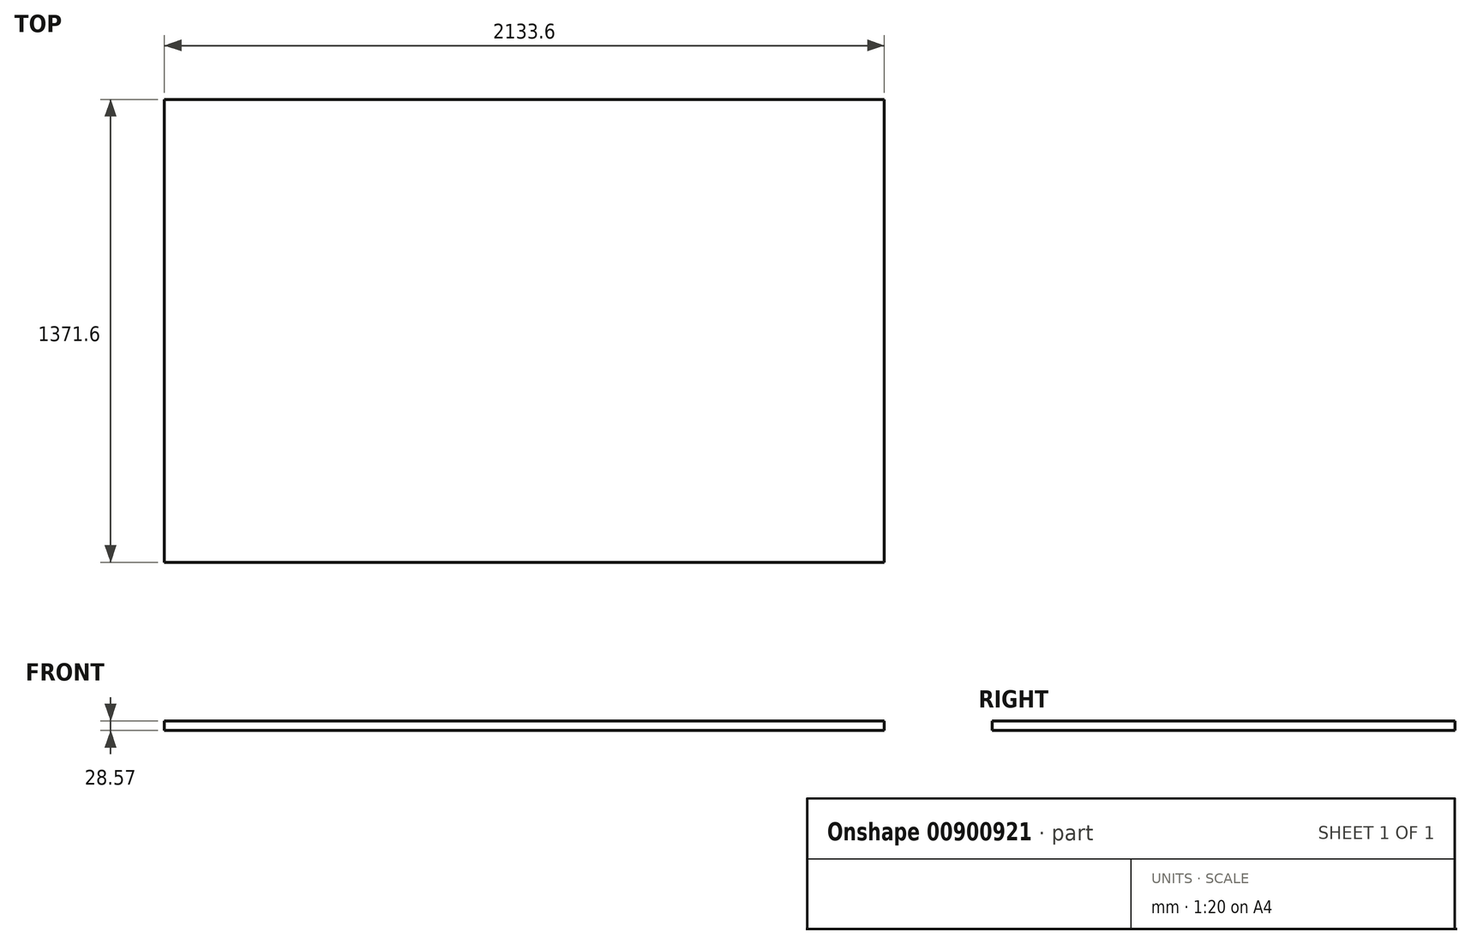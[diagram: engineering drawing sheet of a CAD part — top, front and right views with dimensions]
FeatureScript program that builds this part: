
annotation { "Feature Type Name" : "Feature", "Feature Type Description" : "" }
export const myFeature = defineFeature(function(context is Context, id is Id, definition is map)
    precondition{}
    {
        {
            var Q0;
            Q0=qCreatedBy(makeId("Top.planeOp"),FACE);
            var sketch = newSketch(context, id + "F0", { "sketchPlane" : qUnion([Q0])});
            skLineSegment(sketch, "E0.bottom", {"start": v(1066.8, 685.8) * mm, "end": v(-1066.8, 685.8) * mm});
            skLineSegment(sketch, "E0.top", {"start": v(1066.8, -685.8) * mm, "end": v(-1066.8, -685.8) * mm});
            skLineSegment(sketch, "E0.left", {"start": v(1066.8, 685.8) * mm, "end": v(1066.8, -685.8) * mm});
            skLineSegment(sketch, "E0.right", {"start": v(-1066.8, 685.8) * mm, "end": v(-1066.8, -685.8) * mm});
            skPoint(sketch, "E0.middle", {"position": v(0, 0) * mm});
            skSolve(sketch);
        }
        {
            var Q0;
            Q0=makeQuery(id+"F0.imprint","IMPRINT",FACE,{"disambiguationData":[TD([[makeQuery(id+"F0.imprint","IMPRINT",EDGE,{"derivedFrom":sQuery(id+"F0.wireOp",EDGE,"E0.bottom")}),1.0]])]});
            extrude(context, id + "F1", {"entities" : qUnion([Q0]), "depth" : 28.57 * mm, "offsetDistance" : 25.4 * mm});
        }
    });
